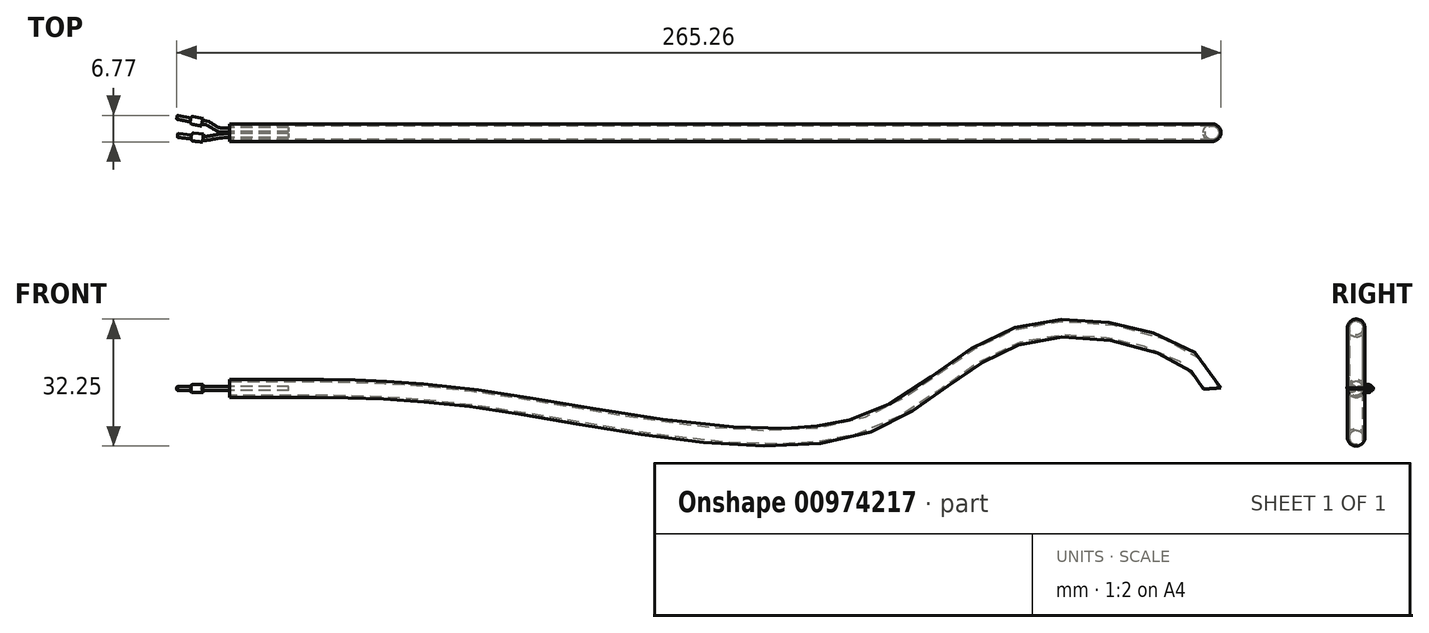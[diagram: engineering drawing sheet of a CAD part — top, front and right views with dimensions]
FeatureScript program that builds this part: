
annotation { "Feature Type Name" : "Feature", "Feature Type Description" : "" }
export const myFeature = defineFeature(function(context is Context, id is Id, definition is map)
    precondition{}
    {
        {
            var Q0;
            Q0=qCreatedBy(makeId("Front.planeOp"),FACE);
            var sketch = newSketch(context, id + "F0", { "sketchPlane" : qUnion([Q0])});
            skFitSpline(sketch, "E0", {"points": [v(0, 0) * mm, v(23.22, 0) * mm, v(68.62, -3.41) * mm, v(160.46, -9.45) * mm, v(205.79, 14.79) * mm, v(249.57, 0) * mm], "startDerivative": vector(171.98, 0) * mm, "endDerivative": vector(10.04, -145.8) * mm});
            skSolve(sketch);
        }
        {
            var Q0;
            Q0=qCreatedBy(makeId("Right.planeOp"),FACE);
            var sketch = newSketch(context, id + "F1", { "sketchPlane" : qUnion([Q0])});
            skCircle(sketch, "E1", {"center": v(0, 0) * mm, "radius": 2.25 * mm});
            skSolve(sketch);
        }
        {
            var Q0;
            Q0=makeQuery(id+"F1.imprint","IMPRINT",FACE,{"disambiguationData":[TD([[makeQuery(id+"F1.imprint","IMPRINT",EDGE,{"derivedFrom":sQuery(id+"F1.wireOp",EDGE,"E1")}),1.0]])]});
            var Q1;
            Q1=sQuery(id+"F0.wireOp",EDGE,"E0");
            sweep(context, id + "F2", {"profiles" : qUnion([Q0]), "path" : qUnion([Q1])});
        }
        {
            var Q0;
            Q0=makeQuery(id+"F2.opSweep","CAP_FACE",FACE,{"disambiguationData":[OSD([sQuery(id+"F0.wireOp",VERTEX,"E0.start"),sQuery(id+"F1.wireOp",EDGE,"E1")])],"isStart":true});
            var Q1;
            Q1=makeQuery(id+"F2.opSweep","CAP_FACE",FACE,{"disambiguationData":[OSD([sQuery(id+"F0.wireOp",VERTEX,"E0.end"),sQuery(id+"F1.wireOp",EDGE,"E1")])],"isStart":false});
            shell(context, id + "F3", {"entities" : qUnion([Q0, Q1]), "thickness" : 0.5 * mm});
        }
        {
            var Q0;
            Q0=qCreatedBy(makeId("Right.planeOp"),FACE);
            var sketch = newSketch(context, id + "F4", { "sketchPlane" : qUnion([Q0])});
            skCircle(sketch, "E2", {"center": v(0.75, 0) * mm, "radius": 0.5 * mm});
            skCircle(sketch, "E3", {"center": v(-0.75, 0) * mm, "radius": 0.5 * mm});
            skSolve(sketch);
        }
        {
            var Q0;
            Q0=qCreatedBy(makeId("Top.planeOp"),FACE);
            var sketch = newSketch(context, id + "F5", { "sketchPlane" : qUnion([Q0])});
            skFitSpline(sketch, "E4", {"points": [v(0, 0.75) * mm, v(-3, 0.9) * mm, v(-5.41, 2.3) * mm, v(-7, 2.65) * mm], "startDerivative": vector(-8.39, -1) * mm, "endDerivative": vector(-5.7, 0.46) * mm});
            skFitSpline(sketch, "E5", {"points": [v(0, -0.76) * mm, v(-2.75, -0.9) * mm, v(-5.7, -1.42) * mm, v(-6.78, -1.4) * mm], "startDerivative": vector(-7.03, -0.02) * mm, "endDerivative": vector(-3.97, 0.42) * mm});
            skSolve(sketch);
        }
        {
            var Q0;
            Q0=makeQuery(id+"F4.imprint","IMPRINT",FACE,{"disambiguationData":[TD([[makeQuery(id+"F4.imprint","IMPRINT",EDGE,{"derivedFrom":sQuery(id+"F4.wireOp",EDGE,"E2")}),1.0]])]});
            var Q1;
            Q1=sQuery(id+"F5.wireOp",EDGE,"E4");
            sweep(context, id + "F6", {"profiles" : qUnion([Q0]), "path" : qUnion([Q1])});
        }
        {
            var Q0;
            Q0=makeQuery(id+"F4.imprint","IMPRINT",FACE,{"disambiguationData":[TD([[makeQuery(id+"F4.imprint","IMPRINT",EDGE,{"derivedFrom":sQuery(id+"F4.wireOp",EDGE,"E3")}),1.0]])]});
            var Q1;
            Q1=sQuery(id+"F4.wireOp",EDGE,"E3");
            var Q2;
            Q2=sQuery(id+"F5.wireOp",EDGE,"E5");
            sweep(context, id + "F7", {"profiles" : qUnion([Q0]), "surfaceProfiles" : qUnion([Q1]), "path" : qUnion([Q2])});
        }
        {
            var Q0;
            Q0=makeQuery(id+"F4.imprint","IMPRINT",FACE,{"disambiguationData":[TD([[makeQuery(id+"F4.imprint","IMPRINT",EDGE,{"derivedFrom":sQuery(id+"F4.wireOp",EDGE,"E3")}),1.0]])]});
            var Q1;
            Q1=sQuery(id+"F4.wireOp",EDGE,"E3");
            extrude(context, id + "F8", {"entities" : qUnion([Q0]), "operationType" : NewBodyOperationType.ADD, "surfaceEntities" : qUnion([Q1]), "depth" : 15 * mm, "offsetDistance" : 25 * mm});
        }
        {
            var Q0;
            Q0=makeQuery(id+"F4.imprint","IMPRINT",FACE,{"disambiguationData":[TD([[makeQuery(id+"F4.imprint","IMPRINT",EDGE,{"derivedFrom":sQuery(id+"F4.wireOp",EDGE,"E2")}),1.0]])]});
            extrude(context, id + "F9", {"entities" : qUnion([Q0]), "operationType" : NewBodyOperationType.ADD, "depth" : 15 * mm, "offsetDistance" : 25 * mm});
        }
        {
            var Q0;
            Q0=makeQuery(id+"F6.opSweep","CAP_FACE",FACE,{"disambiguationData":[OSD([sQuery(id+"F4.wireOp",EDGE,"E2"),sQuery(id+"F5.wireOp",VERTEX,"E4.end")])],"isStart":false});
            var sketch = newSketch(context, id + "F10", { "sketchPlane" : qUnion([Q0])});
            skCircle(sketch, "E6", {"center": v(-1.21, 0) * mm, "radius": 1 * mm});
            skSolve(sketch);
        }
        {
            var Q0;
            Q0 = qSketchRegion(id + "F10", true);
            extrude(context, id + "F11", {"entities" : qUnion([Q0]), "depth" : 3 * mm, "offsetDistance" : 25 * mm});
        }
        {
            var Q0;
            Q0=makeQuery(id+"F11.opExtrude","CAP_EDGE",EDGE,{"disambiguationData":[OSD([sQuery(id+"F10.wireOp",EDGE,"E6")])],"isStart":false});
            fillet(context, id + "F12", {"entities" : qUnion([Q0]), "tangentPropagation" : true, "radius" : 0.5 * mm, "defaultsChanged" : true, "vertexSettings" : [], "allowEdgeOverflow" : false});
        }
        {
            var Q0;
            Q0=makeQuery(id+"F11.opExtrude","CAP_FACE",FACE,{"disambiguationData":[OSD([sQuery(id+"F10.wireOp",EDGE,"E6")])],"isStart":false});
            var sketch = newSketch(context, id + "F13", { "sketchPlane" : qUnion([Q0])});
            skCircle(sketch, "E7", {"center": v(-1.21, 0) * mm, "radius": 0.5 * mm});
            skSolve(sketch);
        }
        {
            var Q0;
            Q0 = qSketchRegion(id + "F13", true);
            extrude(context, id + "F14", {"entities" : qUnion([Q0]), "depth" : 3.5 * mm, "offsetDistance" : 25 * mm});
        }
        {
            var Q0;
            Q0=makeQuery(id+"F14.opExtrude","CAP_EDGE",EDGE,{"disambiguationData":[OSD([sQuery(id+"F13.wireOp",EDGE,"E7")])],"isStart":false});
            fillet(context, id + "F15", {"entities" : qUnion([Q0]), "tangentPropagation" : true, "radius" : 0.2 * mm, "defaultsChanged" : true, "vertexSettings" : [], "allowEdgeOverflow" : false});
        }
        {
            var Q0;
            Q0=makeQuery(id+"F7.opSweep","CAP_FACE",FACE,{"disambiguationData":[OSD([sQuery(id+"F4.wireOp",EDGE,"E3"),sQuery(id+"F5.wireOp",VERTEX,"E5.end")])],"isStart":false});
            var sketch = newSketch(context, id + "F16", { "sketchPlane" : qUnion([Q0])});
            skCircle(sketch, "E8", {"center": v(2.12, 0) * mm, "radius": 1 * mm});
            skSolve(sketch);
        }
        {
            var Q0;
            Q0 = qSketchRegion(id + "F16", true);
            extrude(context, id + "F17", {"entities" : qUnion([Q0]), "depth" : 3 * mm, "offsetDistance" : 25 * mm});
        }
        {
            var Q0;
            Q0=makeQuery(id+"F17.opExtrude","CAP_EDGE",EDGE,{"disambiguationData":[OSD([sQuery(id+"F16.wireOp",EDGE,"E8")])],"isStart":false});
            fillet(context, id + "F18", {"entities" : qUnion([Q0]), "tangentPropagation" : true, "radius" : 0.5 * mm, "defaultsChanged" : true, "vertexSettings" : [], "allowEdgeOverflow" : false});
        }
        {
            var Q0;
            Q0=makeQuery(id+"F17.opExtrude","CAP_FACE",FACE,{"disambiguationData":[OSD([sQuery(id+"F16.wireOp",EDGE,"E8")])],"isStart":false});
            var sketch = newSketch(context, id + "F19", { "sketchPlane" : qUnion([Q0])});
            skCircle(sketch, "E9", {"center": v(2.12, 0) * mm, "radius": 0.5 * mm});
            skSolve(sketch);
        }
        {
            var Q0;
            Q0 = qSketchRegion(id + "F19", true);
            extrude(context, id + "F20", {"entities" : qUnion([Q0]), "depth" : 3.5 * mm, "offsetDistance" : 25 * mm});
        }
        {
            var Q0;
            Q0=makeQuery(id+"F20.opExtrude","CAP_EDGE",EDGE,{"disambiguationData":[OSD([sQuery(id+"F19.wireOp",EDGE,"E9")])],"isStart":false});
            fillet(context, id + "F21", {"entities" : qUnion([Q0]), "tangentPropagation" : true, "radius" : 0.2 * mm, "defaultsChanged" : true, "vertexSettings" : [], "allowEdgeOverflow" : false});
        }
    });
